# Revit family: Seating-LAMMHULTS-PENNE-Chair
name_source: partatom
category: Furniture
revit_build: Autodesk Revit 2015 (Build: 20160512_0715(x64)
units: mm (PartAtom-declared; Revit-internal decimal feet)

## types (4) — shared parameters
Assembly Code = E2020
Depth = 500 mm  [stored 1.64042 ft]
Description = *Please enter mtrl description here for use in mto*
Height = 790 mm  [stored 2.59186 ft]
Keynote = 46.B
Legs Material = Plastic - Black
Manufacturer = LAMMHULTS
Model = PENNE
URL = www.lammhults.se
Width = 510 mm  [stored 1.67323 ft]

## per-type parameters (varying)
| type | Back Material | Frame Material | Seat Material | Weight |
| Plastic-Seat | Plastic - Black | Colour - Coated - Black | Plastic - Black | 4.1 |
| Plastic-Seat-AluFrame | Plastic - Black | Metall - Aluminium - Blank | Plastic - Black | 4.9 |
| Wooden-Seat | Wood - Veneer - Ash | Wood - Veneer - Ash | Wood - Veneer - Ash | 3.1 |
| Wooden-Seat-Aluframe | Wood - Veneer - Oak | Metall - Aluminium - Blank | Wood - Veneer - Oak | 3.9 |

note: [stored X ft] marks values corroborated as IEEE doubles in the binary element streams (Revit-internal decimal feet)

## geometry (parser evidence)
native form markers: Blend x16, Sweep x2
no freeform markers — native parametric forms only
